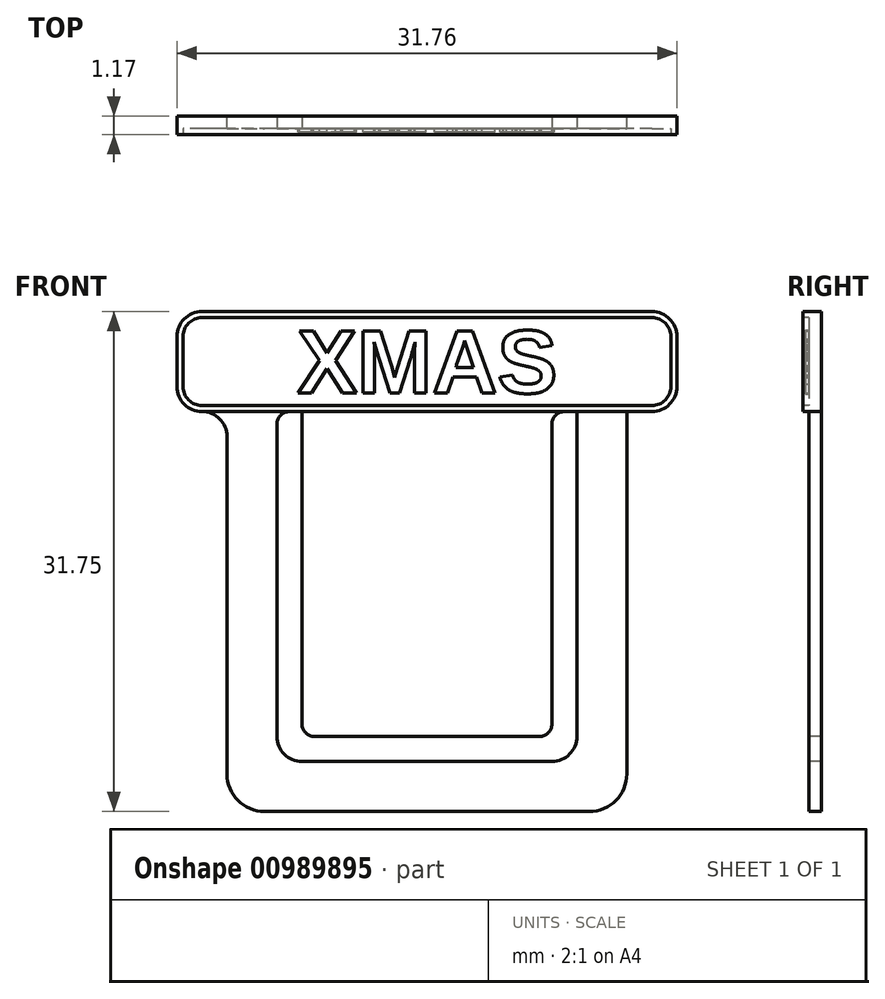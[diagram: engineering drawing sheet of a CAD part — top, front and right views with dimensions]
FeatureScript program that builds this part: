
annotation { "Feature Type Name" : "Feature", "Feature Type Description" : "" }
export const myFeature = defineFeature(function(context is Context, id is Id, definition is map)
    precondition{}
    {
        {
            var Q0;
            Q0=qCreatedBy(makeId("Front.planeOp"),FACE);
            var sketch = newSketch(context, id + "F0", { "sketchPlane" : qUnion([Q0])});
            skLineSegment(sketch, "E0.bottom", {"start": v(12.7, 12.7) * mm, "end": v(-12.7, 12.7) * mm});
            skLineSegment(sketch, "E0.top", {"start": v(12.7, -12.7) * mm, "end": v(-12.7, -12.7) * mm});
            skLineSegment(sketch, "E0.left", {"start": v(12.7, 12.7) * mm, "end": v(12.7, -12.7) * mm});
            skLineSegment(sketch, "E0.right", {"start": v(-12.7, 12.7) * mm, "end": v(-12.7, -12.7) * mm});
            skPoint(sketch, "E0.middle", {"position": v(0, 0) * mm});
            skSolve(sketch);
        }
        {
            var Q0;
            Q0=makeQuery(id+"F0.imprint","IMPRINT",FACE,{"disambiguationData":[TD([[makeQuery(id+"F0.imprint","IMPRINT",EDGE,{"derivedFrom":sQuery(id+"F0.wireOp",EDGE,"E0.bottom")}),1.0]])]});
            extrude(context, id + "F1", {"entities" : qUnion([Q0]), "depth" : 0.8 * mm, "offsetDistance" : 25.4 * mm});
        }
        {
            var Q0;
            Q0=makeQuery(id+"F1.opExtrude","SWEPT_EDGE",EDGE,{"disambiguationData":[OSD([sQuery(id+"F0.wireOp",EDGE,"E0.top"),sQuery(id+"F0.wireOp",EDGE,"E0.left")])]});
            var Q1;
            Q1=makeQuery(id+"F1.opExtrude","SWEPT_EDGE",EDGE,{"disambiguationData":[OSD([sQuery(id+"F0.wireOp",EDGE,"E0.top"),sQuery(id+"F0.wireOp",EDGE,"E0.right")])]});
            fillet(context, id + "F2", {"entities" : qUnion([Q0, Q1]), "radius" : 2.38 * mm, "tangentPropagation" : true, "allowEdgeOverflow" : false});
        }
        {
            var Q0;
            Q0=makeQuery(id+"F1.opExtrude","CAP_FACE",FACE,{"disambiguationData":[OSD([sQuery(id+"F0.wireOp",EDGE,"E0.bottom"),sQuery(id+"F0.wireOp",EDGE,"E0.top"),sQuery(id+"F0.wireOp",EDGE,"E0.left"),sQuery(id+"F0.wireOp",EDGE,"E0.right")])],"isStart":false});
            var sketch = newSketch(context, id + "F3", { "sketchPlane" : qUnion([Q0])});
            skLineSegment(sketch, "E1.bottom", {"start": v(9.52, 12.7) * mm, "end": v(-9.53, 12.7) * mm});
            skLineSegment(sketch, "E1.top", {"start": v(9.53, -9.53) * mm, "end": v(-9.52, -9.53) * mm});
            skLineSegment(sketch, "E1.left", {"start": v(9.52, 12.7) * mm, "end": v(9.53, -9.53) * mm});
            skLineSegment(sketch, "E1.right", {"start": v(-9.53, 12.7) * mm, "end": v(-9.52, -9.53) * mm});
            skPoint(sketch, "E1.middle", {"position": v(0, 0) * mm});
            skSolve(sketch);
        }
        {
            var Q0;
            Q0=makeQuery(id+"F3.imprint","IMPRINT",FACE,{"disambiguationData":[TD([[makeQuery(id+"F3.imprint","IMPRINT",EDGE,{"derivedFrom":sQuery(id+"F3.wireOp",EDGE,"E1.bottom")}),1.0]])]});
            extrude(context, id + "F4", {"entities" : qUnion([Q0]), "operationType" : NewBodyOperationType.REMOVE, "oppositeDirection" : true, "depth" : 4.93 * mm, "offsetDistance" : 25.4 * mm});
        }
        {
            var Q0;
            Q0=makeQuery(id+"F1.opExtrude","CAP_FACE",FACE,{"disambiguationData":[OSD([sQuery(id+"F0.wireOp",EDGE,"E0.bottom"),sQuery(id+"F0.wireOp",EDGE,"E0.top"),sQuery(id+"F0.wireOp",EDGE,"E0.left"),sQuery(id+"F0.wireOp",EDGE,"E0.right")])],"isStart":false});
            var sketch = newSketch(context, id + "F5", { "sketchPlane" : qUnion([Q0])});
            skLineSegment(sketch, "E2.bottom", {"start": v(-15.88, 12.7) * mm, "end": v(15.88, 12.7) * mm});
            skLineSegment(sketch, "E2.top", {"start": v(-15.88, 19.05) * mm, "end": v(15.88, 19.05) * mm});
            skLineSegment(sketch, "E2.left", {"start": v(-15.88, 12.7) * mm, "end": v(-15.88, 19.05) * mm});
            skLineSegment(sketch, "E2.right", {"start": v(15.87, 12.7) * mm, "end": v(15.87, 19.05) * mm});
            skSolve(sketch);
        }
        {
            var Q0;
            Q0=makeQuery(id+"F5.imprint","IMPRINT",FACE,{"disambiguationData":[TD([[makeQuery(id+"F5.imprint","IMPRINT",EDGE,{"derivedFrom":sQuery(id+"F5.wireOp",EDGE,"E2.top")}),-1.0]])]});
            extrude(context, id + "F6", {"entities" : qUnion([Q0]), "operationType" : NewBodyOperationType.ADD, "oppositeDirection" : true, "depth" : 0.8 * mm, "offsetDistance" : 25.4 * mm});
        }
        {
            var Q0;
            Q0=makeQuery(id+"F6.opExtrude","SWEPT_EDGE",EDGE,{"disambiguationData":[OSD([sQuery(id+"F5.wireOp",EDGE,"E2.top"),sQuery(id+"F5.wireOp",EDGE,"E2.left")])]});
            var Q1;
            Q1=makeQuery(id+"F6.opExtrude","SWEPT_EDGE",EDGE,{"disambiguationData":[OSD([sQuery(id+"F5.wireOp",EDGE,"E2.top"),sQuery(id+"F5.wireOp",EDGE,"E2.right")])]});
            var Q2;
            Q2=makeQuery(id+"F6.opExtrude","SWEPT_EDGE",EDGE,{"disambiguationData":[OSD([sQuery(id+"F5.wireOp",EDGE,"E2.bottom"),sQuery(id+"F5.wireOp",EDGE,"E2.right")])]});
            var Q3;
            Q3=makeQuery(id+"F1.opExtrude","SWEPT_EDGE",EDGE,{"disambiguationData":[OSD([sQuery(id+"F0.wireOp",EDGE,"E0.bottom"),sQuery(id+"F0.wireOp",EDGE,"E0.left")])]});
            var Q4;
            Q4=makeQuery(id+"F6.opExtrude","SWEPT_EDGE",EDGE,{"disambiguationData":[OSD([sQuery(id+"F5.wireOp",EDGE,"E2.bottom"),sQuery(id+"F5.wireOp",EDGE,"E2.left")])]});
            var Q5;
            Q5=makeQuery(id+"F1.opExtrude","SWEPT_EDGE",EDGE,{"disambiguationData":[OSD([sQuery(id+"F0.wireOp",EDGE,"E0.bottom"),sQuery(id+"F0.wireOp",EDGE,"E0.right")])]});
            fillet(context, id + "F7", {"entities" : qUnion([Q0, Q1, Q2, Q3, Q4, Q5]), "radius" : 1.59 * mm, "tangentPropagation" : true, "allowEdgeOverflow" : false});
        }
        {
            var Q0;
            Q0=makeQuery(id+"F4.boolean.opBoolean","COPY",EDGE,{"derivedFrom":makeQuery(id+"F4.opExtrude","SWEPT_EDGE",EDGE,{"disambiguationData":[OSD([sQuery(id+"F3.wireOp",EDGE,"E1.top"),sQuery(id+"F3.wireOp",EDGE,"E1.right")])]})});
            var Q1;
            Q1=makeQuery(id+"F4.boolean.opBoolean","COPY",EDGE,{"derivedFrom":makeQuery(id+"F4.opExtrude","SWEPT_EDGE",EDGE,{"disambiguationData":[OSD([sQuery(id+"F3.wireOp",EDGE,"E1.top"),sQuery(id+"F3.wireOp",EDGE,"E1.left")])]})});
            fillet(context, id + "F8", {"entities" : qUnion([Q0, Q1]), "radius" : 1.59 * mm, "tangentPropagation" : true, "allowEdgeOverflow" : false});
        }
        {
            var Q0;
            Q0=makeQuery(id+"F6.boolean.opBoolean","MERGE",FACE,{"derivedFrom":[makeQuery(id+"F1.opExtrude","CAP_FACE",FACE,{"disambiguationData":[OSD([sQuery(id+"F0.wireOp",EDGE,"E0.bottom"),sQuery(id+"F0.wireOp",EDGE,"E0.top"),sQuery(id+"F0.wireOp",EDGE,"E0.left"),sQuery(id+"F0.wireOp",EDGE,"E0.right")])],"isStart":false}),makeQuery(id+"F6.opExtrude","CAP_FACE",FACE,{"disambiguationData":[OSD([sQuery(id+"F5.wireOp",EDGE,"E2.bottom"),sQuery(id+"F5.wireOp",EDGE,"E2.top"),sQuery(id+"F5.wireOp",EDGE,"E2.left"),sQuery(id+"F5.wireOp",EDGE,"E2.right")])],"isStart":true})]});
            var sketch = newSketch(context, id + "F9", { "sketchPlane" : qUnion([Q0])});
            skLineSegment(sketch, "E3.bottom", {"start": v(-7.94, 12.7) * mm, "end": v(7.94, 12.7) * mm});
            skLineSegment(sketch, "E3.top", {"start": v(-7.94, -7.94) * mm, "end": v(7.94, -7.94) * mm});
            skLineSegment(sketch, "E3.left", {"start": v(-7.94, 12.7) * mm, "end": v(-7.94, -7.94) * mm});
            skLineSegment(sketch, "E3.right", {"start": v(7.94, 12.7) * mm, "end": v(7.94, -7.94) * mm});
            skSolve(sketch);
        }
        {
            var Q0;
            Q0=makeQuery(id+"F9.imprint","IMPRINT",FACE,{"disambiguationData":[TD([[makeQuery(id+"F9.imprint","IMPRINT",EDGE,{"derivedFrom":sQuery(id+"F9.wireOp",EDGE,"E3.bottom")}),1.0]])]});
            extrude(context, id + "F10", {"entities" : qUnion([Q0]), "operationType" : NewBodyOperationType.ADD, "oppositeDirection" : true, "depth" : 0.8 * mm, "offsetDistance" : 25.4 * mm});
        }
        {
            var Q0;
            Q0=makeQuery(id+"F10.opExtrude","SWEPT_EDGE",EDGE,{"disambiguationData":[OSD([sQuery(id+"F5.wireOp",EDGE,"E2.bottom"),sQuery(id+"F9.wireOp",EDGE,"E3.bottom"),sQuery(id+"F9.wireOp",EDGE,"E3.left")])]});
            var Q1;
            Q1=makeQuery(id+"F4.boolean.opBoolean","COPY",EDGE,{"derivedFrom":makeQuery(id+"F4.opExtrude","SWEPT_EDGE",EDGE,{"disambiguationData":[OSD([sQuery(id+"F0.wireOp",EDGE,"E0.bottom"),sQuery(id+"F3.wireOp",EDGE,"E1.bottom"),sQuery(id+"F3.wireOp",EDGE,"E1.right")])]})});
            var Q2;
            Q2=makeQuery(id+"F10.opExtrude","SWEPT_EDGE",EDGE,{"disambiguationData":[OSD([sQuery(id+"F5.wireOp",EDGE,"E2.bottom"),sQuery(id+"F9.wireOp",EDGE,"E3.bottom"),sQuery(id+"F9.wireOp",EDGE,"E3.right")])]});
            var Q3;
            Q3=makeQuery(id+"F4.boolean.opBoolean","COPY",EDGE,{"derivedFrom":makeQuery(id+"F4.opExtrude","SWEPT_EDGE",EDGE,{"disambiguationData":[OSD([sQuery(id+"F0.wireOp",EDGE,"E0.bottom"),sQuery(id+"F3.wireOp",EDGE,"E1.bottom"),sQuery(id+"F3.wireOp",EDGE,"E1.left")])]})});
            fillet(context, id + "F11", {"entities" : qUnion([Q0, Q1, Q2, Q3]), "radius" : 0.8 * mm, "tangentPropagation" : true, "allowEdgeOverflow" : false});
        }
        {
            var Q0;
            Q0=makeQuery(id+"F10.opExtrude","SWEPT_EDGE",EDGE,{"disambiguationData":[OSD([sQuery(id+"F9.wireOp",EDGE,"E3.top"),sQuery(id+"F9.wireOp",EDGE,"E3.left")])]});
            var Q1;
            Q1=makeQuery(id+"F10.opExtrude","SWEPT_EDGE",EDGE,{"disambiguationData":[OSD([sQuery(id+"F9.wireOp",EDGE,"E3.top"),sQuery(id+"F9.wireOp",EDGE,"E3.right")])]});
            fillet(context, id + "F12", {"entities" : qUnion([Q0, Q1]), "radius" : 0.8 * mm, "tangentPropagation" : true, "allowEdgeOverflow" : false});
        }
        {
            var Q0;
            Q0=makeQuery(id+"F10.boolean.opBoolean","MERGE",FACE,{"derivedFrom":[makeQuery(id+"F6.boolean.opBoolean","MERGE",FACE,{"derivedFrom":[makeQuery(id+"F1.opExtrude","CAP_FACE",FACE,{"disambiguationData":[OSD([sQuery(id+"F0.wireOp",EDGE,"E0.bottom"),sQuery(id+"F0.wireOp",EDGE,"E0.top"),sQuery(id+"F0.wireOp",EDGE,"E0.left"),sQuery(id+"F0.wireOp",EDGE,"E0.right")])],"isStart":false}),makeQuery(id+"F6.opExtrude","CAP_FACE",FACE,{"disambiguationData":[OSD([sQuery(id+"F5.wireOp",EDGE,"E2.bottom"),sQuery(id+"F5.wireOp",EDGE,"E2.top"),sQuery(id+"F5.wireOp",EDGE,"E2.left"),sQuery(id+"F5.wireOp",EDGE,"E2.right")])],"isStart":true})]}),makeQuery(id+"F10.opExtrude","CAP_FACE",FACE,{"disambiguationData":[OSD([sQuery(id+"F9.wireOp",EDGE,"E3.bottom"),sQuery(id+"F9.wireOp",EDGE,"E3.top"),sQuery(id+"F9.wireOp",EDGE,"E3.left"),sQuery(id+"F9.wireOp",EDGE,"E3.right")])],"isStart":true})]});
            var sketch = newSketch(context, id + "F13", { "sketchPlane" : qUnion([Q0])});
            skArc(sketch, "E4.0", {"start": v(-14.29, 19.05) * mm, "mid": v(-15.41, 18.59) * mm, "end": v(-15.88, 17.46) * mm});
            skLineSegment(sketch, "E5.0", {"start": v(-15.88, 14.29) * mm, "end": v(-15.88, 17.46) * mm});
            skArc(sketch, "E6.0", {"start": v(-15.88, 14.29) * mm, "mid": v(-15.41, 13.16) * mm, "end": v(-14.29, 12.7) * mm});
            skLineSegment(sketch, "E7.0", {"start": v(-14.29, 19.05) * mm, "end": v(14.29, 19.05) * mm});
            skArc(sketch, "E8.0", {"start": v(15.87, 17.46) * mm, "mid": v(15.41, 18.59) * mm, "end": v(14.29, 19.05) * mm});
            skLineSegment(sketch, "E9.0", {"start": v(15.87, 14.29) * mm, "end": v(15.87, 17.46) * mm});
            skArc(sketch, "E10.0", {"start": v(14.29, 12.7) * mm, "mid": v(15.41, 13.16) * mm, "end": v(15.87, 14.29) * mm});
            skLineSegment(sketch, "E11", {"start": v(-14.29, 12.7) * mm, "end": v(14.29, 12.7) * mm});
            skSolve(sketch);
        }
        {
            var Q0;
            Q0=makeQuery(id+"F13.imprint","IMPRINT",FACE,{"disambiguationData":[TD([[makeQuery(id+"F13.imprint","IMPRINT",EDGE,{"derivedFrom":sQuery(id+"F13.wireOp",EDGE,"E4.0")}),1.0]])]});
            extrude(context, id + "F14", {"entities" : qUnion([Q0]), "operationType" : NewBodyOperationType.ADD, "depth" : 0.38 * mm, "offsetDistance" : 25.4 * mm});
        }
        {
            var Q0;
            Q0=makeQuery(id+"F14.opExtrude","CAP_FACE",FACE,{"disambiguationData":[OSD([sQuery(id+"F13.wireOp",EDGE,"E4.0"),sQuery(id+"F13.wireOp",EDGE,"E5.0"),sQuery(id+"F13.wireOp",EDGE,"E6.0"),sQuery(id+"F13.wireOp",EDGE,"E7.0"),sQuery(id+"F13.wireOp",EDGE,"E8.0"),sQuery(id+"F13.wireOp",EDGE,"E9.0"),sQuery(id+"F13.wireOp",EDGE,"E10.0"),sQuery(id+"F13.wireOp",EDGE,"E11")])],"isStart":false});
            var sketch = newSketch(context, id + "F15", { "sketchPlane" : qUnion([Q0])});
            skArc(sketch, "E12.0", {"start": v(-14.29, 19.05) * mm, "mid": v(-15.41, 18.59) * mm, "end": v(-15.88, 17.46) * mm});
            skLineSegment(sketch, "E13.0", {"start": v(-14.29, 19.05) * mm, "end": v(14.29, 19.05) * mm});
            skLineSegment(sketch, "E14.0", {"start": v(-15.88, 14.29) * mm, "end": v(-15.88, 17.46) * mm});
            skArc(sketch, "E15.0", {"start": v(-15.88, 14.29) * mm, "mid": v(-15.41, 13.16) * mm, "end": v(-14.29, 12.7) * mm});
            skLineSegment(sketch, "E16.0", {"start": v(-14.29, 12.7) * mm, "end": v(14.29, 12.7) * mm});
            skArc(sketch, "E17.0", {"start": v(14.29, 12.7) * mm, "mid": v(15.41, 13.16) * mm, "end": v(15.87, 14.29) * mm});
            skArc(sketch, "E18.0", {"start": v(15.87, 17.46) * mm, "mid": v(15.41, 18.59) * mm, "end": v(14.29, 19.05) * mm});
            skArc(sketch, "E19", {"start": v(-14.29, 18.67) * mm, "mid": v(-15.14, 18.32) * mm, "end": v(-15.5, 17.46) * mm});
            skArc(sketch, "E20", {"start": v(-15.5, 14.29) * mm, "mid": v(-15.14, 13.43) * mm, "end": v(-14.29, 13.08) * mm});
            skArc(sketch, "E21", {"start": v(15.5, 17.46) * mm, "mid": v(15.14, 18.32) * mm, "end": v(14.29, 18.67) * mm});
            skArc(sketch, "E22", {"start": v(14.29, 13.08) * mm, "mid": v(15.14, 13.43) * mm, "end": v(15.5, 14.29) * mm});
            skLineSegment(sketch, "E23", {"start": v(-14.29, 19.05) * mm, "end": v(-14.29, 12.7) * mm, "construction": true});
            skLineSegment(sketch, "E24", {"start": v(-15.88, 17.46) * mm, "end": v(15.87, 17.46) * mm, "construction": true});
            skLineSegment(sketch, "E25", {"start": v(14.29, 19.05) * mm, "end": v(14.29, 12.7) * mm, "construction": true});
            skLineSegment(sketch, "E26", {"start": v(15.87, 14.29) * mm, "end": v(-15.88, 14.29) * mm, "construction": true});
            skLineSegment(sketch, "E27", {"start": v(14.29, 18.67) * mm, "end": v(-14.29, 18.67) * mm});
            skLineSegment(sketch, "E28", {"start": v(-15.5, 17.46) * mm, "end": v(-15.5, 14.29) * mm});
            skLineSegment(sketch, "E29", {"start": v(-14.29, 13.08) * mm, "end": v(14.29, 13.08) * mm});
            skLineSegment(sketch, "E30", {"start": v(15.5, 17.46) * mm, "end": v(15.5, 14.29) * mm});
            skSolve(sketch);
        }
        {
            var Q0;
            Q0=makeQuery(id+"F15.imprint","IMPRINT",FACE,{"disambiguationData":[TD([[makeQuery(id+"F15.imprint","IMPRINT",EDGE,{"derivedFrom":sQuery(id+"F15.wireOp",EDGE,"E19")}),1.0]])]});
            var Q1;
            {var subQ0=sQuery(id+"F9.wireOp",EDGE,"E3.right");var subQ1=sQuery(id+"F9.wireOp",EDGE,"E3.top");var subQ3=sQuery(id+"F0.wireOp",EDGE,"E0.bottom");var subQ4=sQuery(id+"F9.wireOp",EDGE,"E3.left");var subQ5=makeQuery(id+"F6.opExtrude","CAP_FACE",FACE,{"disambiguationData":[OSD([sQuery(id+"F5.wireOp",EDGE,"E2.bottom"),sQuery(id+"F5.wireOp",EDGE,"E2.top"),sQuery(id+"F5.wireOp",EDGE,"E2.left"),sQuery(id+"F5.wireOp",EDGE,"E2.right")])],"isStart":true});var subQ6=makeQuery(id+"F1.opExtrude","CAP_FACE",FACE,{"disambiguationData":[OSD([subQ3,sQuery(id+"F0.wireOp",EDGE,"E0.top"),sQuery(id+"F0.wireOp",EDGE,"E0.left"),sQuery(id+"F0.wireOp",EDGE,"E0.right")])],"isStart":false});var subQ7=makeQuery(id+"F10.opExtrude","CAP_FACE",FACE,{"disambiguationData":[OSD([sQuery(id+"F9.wireOp",EDGE,"E3.bottom"),subQ1,subQ4,subQ0])],"isStart":true});Q1=makeQuery(id+"F14.boolean.opBoolean","SPLIT",FACE,{"disambiguationData":[TD([makeQuery(id+"F10.opExtrude","SWEPT_FACE",FACE,{"disambiguationData":[OSD([subQ1])]})])],"derivedFrom":makeQuery(id+"F10.boolean.opBoolean","MERGE",FACE,{"derivedFrom":[makeQuery(id+"F6.boolean.opBoolean","MERGE",FACE,{"derivedFrom":[subQ6,subQ5]}),subQ7]})});}
            extrude(context, id + "F16", {"entities" : qUnion([Q0]), "operationType" : NewBodyOperationType.REMOVE, "endBound" : BoundingType.UP_TO_SURFACE, "oppositeDirection" : true, "depth" : 25.4 * mm, "endBoundEntityFace" : qUnion([Q1]), "offsetDistance" : 25.4 * mm});
        }
        {
            var Q0;
            Q0=qCreatedBy(makeId("Front.planeOp"),FACE);
            var sketch = newSketch(context, id + "F17", { "sketchPlane" : qUnion([Q0])});
            skText(sketch, "E31", { "text": "XMAS", "fontName": "Arimo-Bold.ttf"});
            const initialGuessF17  = {"E31": [-0.00825, 0.01388, 1, 0, 0.00412]};
            skSetInitialGuess(sketch, initialGuessF17);
            skSolve(sketch);
        }
        {
            var Q0;
            Q0=qSketchRegion(id+"F17",true);
            extrude(context, id + "F18", {"entities" : qUnion([Q0]), "operationType" : NewBodyOperationType.ADD, "depth" : 1.02 * mm, "offsetDistance" : 25.4 * mm});
        }
    });
